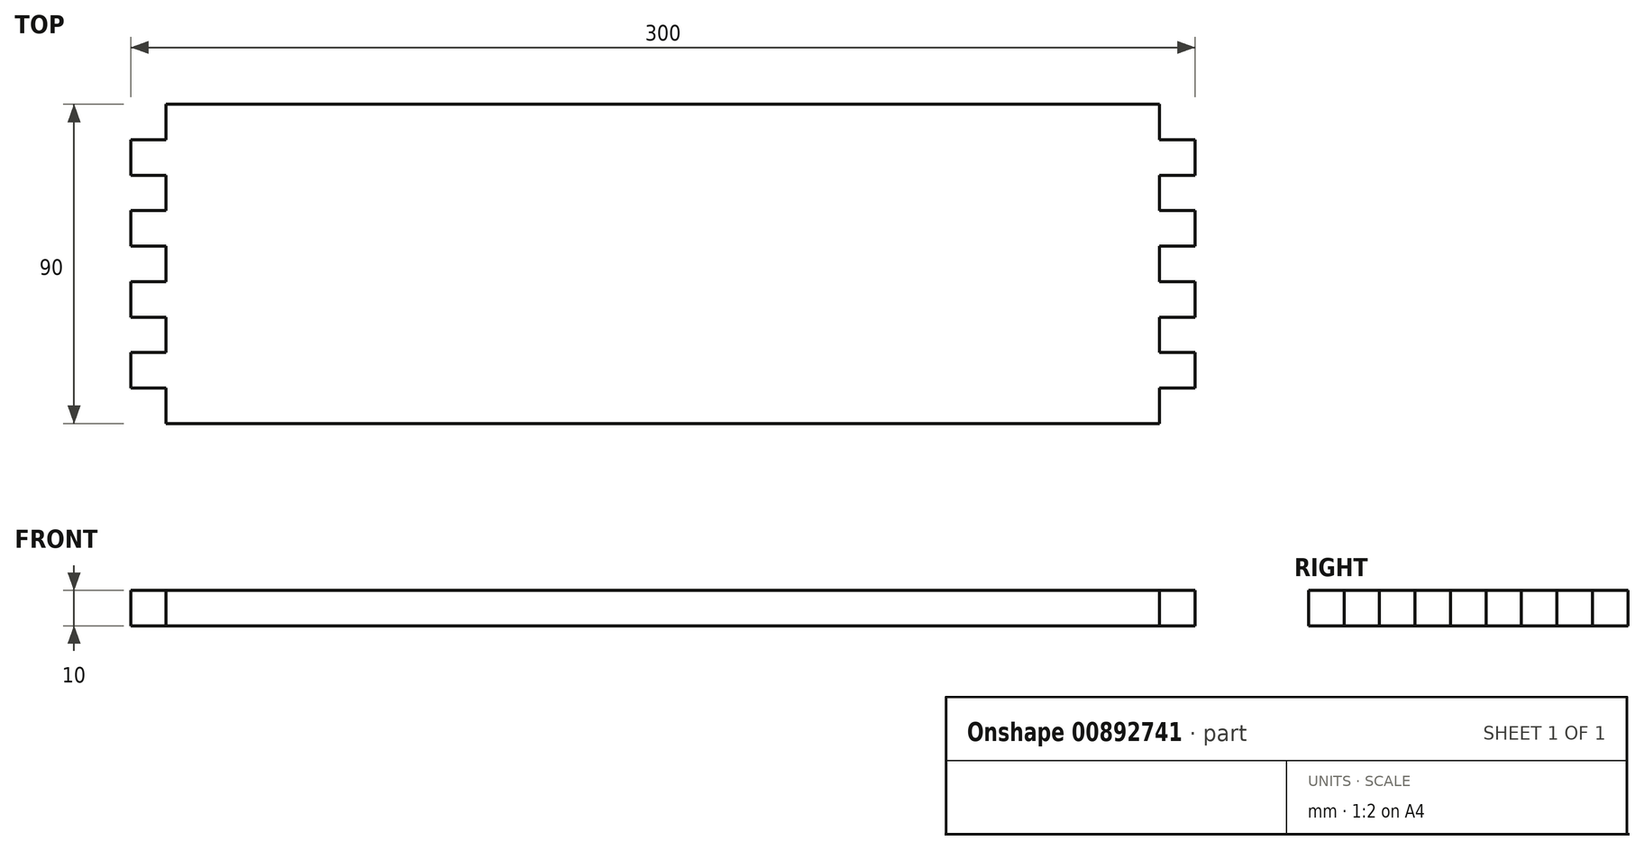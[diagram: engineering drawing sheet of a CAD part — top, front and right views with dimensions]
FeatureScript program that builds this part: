
annotation { "Feature Type Name" : "Feature", "Feature Type Description" : "" }
export const myFeature = defineFeature(function(context is Context, id is Id, definition is map)
    precondition{}
    {
        {
            var Q0;
            Q0=qCreatedBy(makeId("Top.planeOp"),FACE);
            var sketch = newSketch(context, id + "F0", { "sketchPlane" : qUnion([Q0])});
            skLineSegment(sketch, "E0.bottom", {"start": v(140, 45) * mm, "end": v(-140, 45) * mm});
            skLineSegment(sketch, "E0.top", {"start": v(140, -45) * mm, "end": v(-140, -45) * mm});
            skLineSegment(sketch, "E0.left", {"start": v(150, 35) * mm, "end": v(150, 25) * mm});
            skLineSegment(sketch, "E0.right", {"start": v(-150, 35) * mm, "end": v(-150, 25) * mm});
            skPoint(sketch, "E0.middle", {"position": v(0, 0) * mm});
            skLineSegment(sketch, "E1", {"start": v(-140, 45) * mm, "end": v(-140, 35) * mm});
            skLineSegment(sketch, "E2", {"start": v(-150, 35) * mm, "end": v(-140, 35) * mm});
            skLineSegment(sketch, "E3", {"start": v(-150, 25) * mm, "end": v(-140, 25) * mm});
            skLineSegment(sketch, "E4", {"start": v(-150, 15) * mm, "end": v(-140, 15) * mm});
            skLineSegment(sketch, "E5", {"start": v(-150, 5) * mm, "end": v(-140, 5) * mm});
            skPoint(sketch, "E5.endSnap0", {"position": v(-140, 0) * mm});
            skLineSegment(sketch, "E6", {"start": v(-150, -5) * mm, "end": v(-140, -5) * mm});
            skLineSegment(sketch, "E7", {"start": v(-150, -15) * mm, "end": v(-140, -15) * mm});
            skLineSegment(sketch, "E8", {"start": v(-150, -25) * mm, "end": v(-140, -25) * mm});
            skLineSegment(sketch, "E9", {"start": v(-150, -35) * mm, "end": v(-140, -35) * mm});
            skPoint(sketch, "E10.orphan", {"position": v(-150, 45) * mm});
            skLineSegment(sketch, "E11.trimOffspring", {"start": v(-150, 15) * mm, "end": v(-150, 5) * mm});
            skLineSegment(sketch, "E12.trimOffspring", {"start": v(-150, -5) * mm, "end": v(-150, -15) * mm});
            skLineSegment(sketch, "E13.trimOffspring", {"start": v(-150, -25) * mm, "end": v(-150, -35) * mm});
            skLineSegment(sketch, "E14.trimOffspring", {"start": v(-140, -15) * mm, "end": v(-140, -25) * mm});
            skLineSegment(sketch, "E15.trimOffspring", {"start": v(-140, 25) * mm, "end": v(-140, 15) * mm});
            skLineSegment(sketch, "E16.trimOffspring", {"start": v(-140, 5) * mm, "end": v(-140, -5) * mm});
            skLineSegment(sketch, "E17.trimOffspring", {"start": v(-140, -35) * mm, "end": v(-140, -45) * mm});
            skLineSegment(sketch, "E18.MirrorCS", {"start": v(140, 5) * mm, "end": v(140, -5) * mm});
            skLineSegment(sketch, "E19.MirrorCS", {"start": v(150, -5) * mm, "end": v(140, -5) * mm});
            skLineSegment(sketch, "E20.MirrorCS", {"start": v(140, 25) * mm, "end": v(140, 15) * mm});
            skPoint(sketch, "E21.MirrorP", {"position": v(150, 45) * mm});
            skLineSegment(sketch, "E22.MirrorCS", {"start": v(140, -35) * mm, "end": v(140, -45) * mm});
            skLineSegment(sketch, "E23.MirrorCS", {"start": v(150, -25) * mm, "end": v(150, -35) * mm});
            skLineSegment(sketch, "E24.MirrorCS", {"start": v(140, 45) * mm, "end": v(140, 35) * mm});
            skLineSegment(sketch, "E25.MirrorCS", {"start": v(150, 25) * mm, "end": v(140, 25) * mm});
            skLineSegment(sketch, "E26.MirrorCS", {"start": v(150, 5) * mm, "end": v(140, 5) * mm});
            skLineSegment(sketch, "E27.MirrorCS", {"start": v(150, 15) * mm, "end": v(140, 15) * mm});
            skLineSegment(sketch, "E28.MirrorCS", {"start": v(150, -25) * mm, "end": v(140, -25) * mm});
            skLineSegment(sketch, "E29.MirrorCS", {"start": v(150, 35) * mm, "end": v(140, 35) * mm});
            skLineSegment(sketch, "E30.MirrorCS", {"start": v(150, 15) * mm, "end": v(150, 5) * mm});
            skLineSegment(sketch, "E31.MirrorCS", {"start": v(150, -15) * mm, "end": v(140, -15) * mm});
            skLineSegment(sketch, "E32.MirrorCS", {"start": v(150, -5) * mm, "end": v(150, -15) * mm});
            skLineSegment(sketch, "E33.MirrorCS", {"start": v(140, -15) * mm, "end": v(140, -25) * mm});
            skLineSegment(sketch, "E34.MirrorCS", {"start": v(150, -35) * mm, "end": v(140, -35) * mm});
            skPoint(sketch, "E35.MirrorP", {"position": v(140, 0) * mm});
            skPoint(sketch, "E36.orphan", {"position": v(150, -45) * mm});
            skPoint(sketch, "E37.orphan", {"position": v(-150, -45) * mm});
            skSolve(sketch);
        }
        {
            var Q0;
            Q0=makeQuery(id+"F0.imprint","IMPRINT",FACE,{"disambiguationData":[TD([[makeQuery(id+"F0.imprint","IMPRINT",EDGE,{"derivedFrom":sQuery(id+"F0.wireOp",EDGE,"E0.bottom")}),1.0]])]});
            extrude(context, id + "F1", {"entities" : qUnion([Q0]), "depth" : 10 * mm, "offsetDistance" : 25 * mm});
        }
    });
